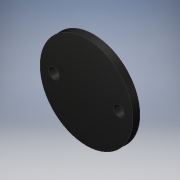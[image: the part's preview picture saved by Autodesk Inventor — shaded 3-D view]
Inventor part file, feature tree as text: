
AUTODESK INVENTOR PART (.ipt)
format: ipt  version: 2019.4 (Build 234330000, 330)  size: 103,936 bytes
history: native  units: mm
features: extrude x1, sketch x1
ambient origin geometry x8: Origin, YZ Plane, XZ Plane, XY Plane, X Axis, Y Axis, Z Axis, Center Point
bodies: Solid1 (feature_tree)
feature tree (2):
  extrude  "Extrusion1"  Depth=1.7mm
  sketch  "Sketch1"  dims[d0=22.0mm d1=15.4mm d2=2.5mm d3=2.5mm d4=1.7mm d5=0.0mm]
